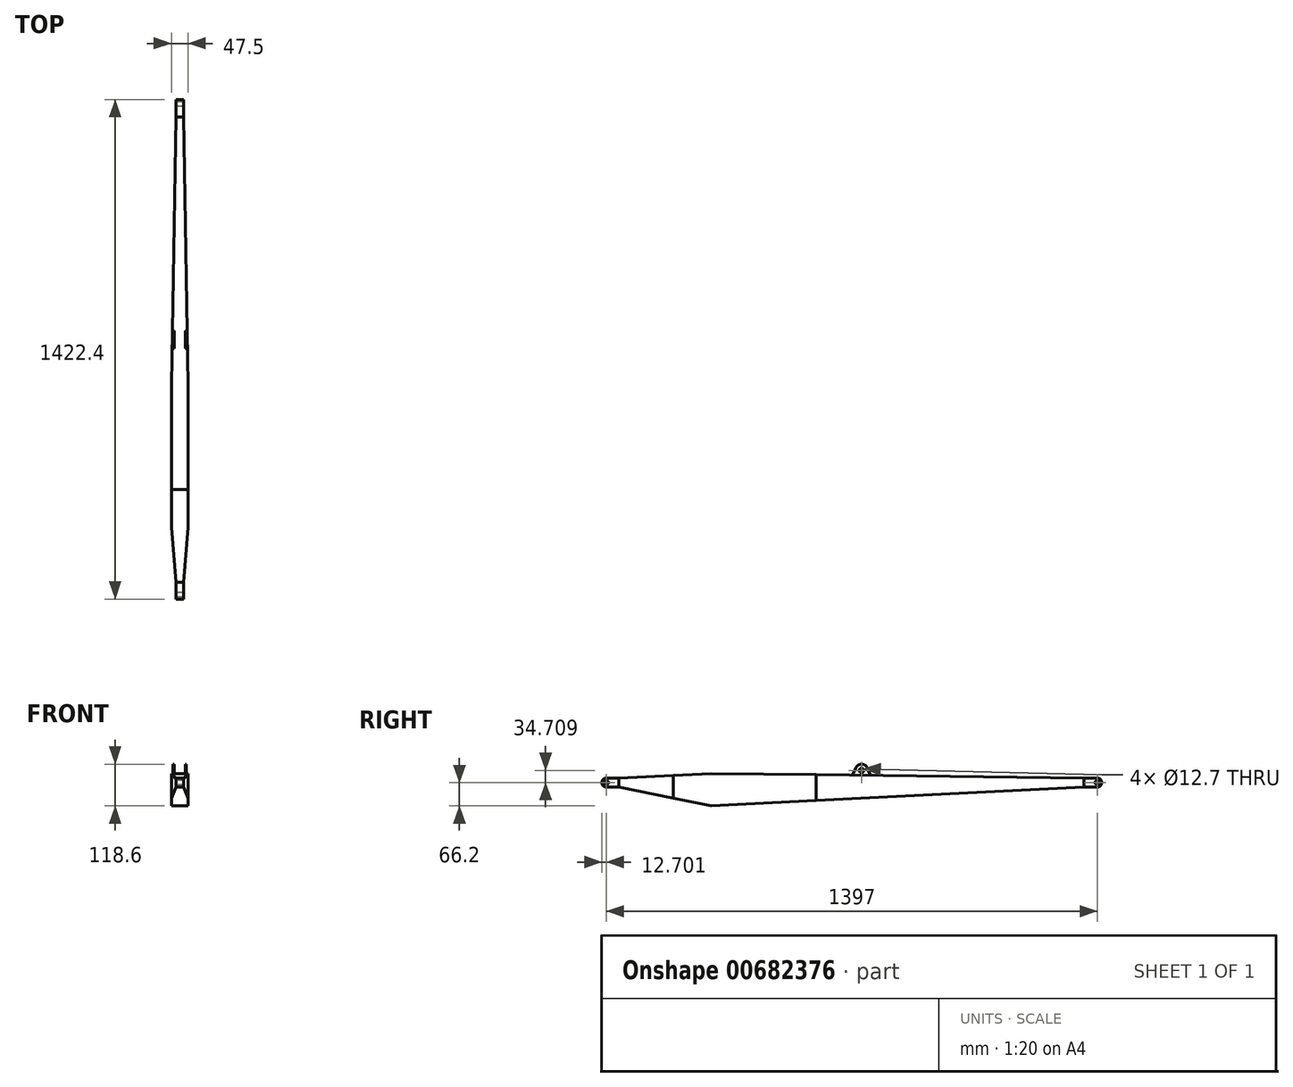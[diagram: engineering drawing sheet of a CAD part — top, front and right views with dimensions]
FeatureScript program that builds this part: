
annotation { "Feature Type Name" : "Feature", "Feature Type Description" : "" }
export const myFeature = defineFeature(function(context is Context, id is Id, definition is map)
    precondition{}
    {
        {
            var Q0;
            Q0=qCreatedBy(makeId("Right.planeOp"),FACE);
            var sketch = newSketch(context, id + "F0", { "sketchPlane" : qUnion([Q0])});
            skCircle(sketch, "E0", {"center": v(-27.04, 0) * mm, "radius": 6.35 * mm});
            skLineSegment(sketch, "E1", {"start": v(-27.04, 0) * mm, "end": v(1369.96, 0) * mm, "construction": true});
            skCircle(sketch, "E2", {"center": v(1369.96, 0) * mm, "radius": 6.35 * mm});
            skArc(sketch, "E3", {"start": v(-27.04, 12.7) * mm, "mid": v(-39.74, 0) * mm, "end": v(-27.04, -12.7) * mm});
            skArc(sketch, "E4", {"start": v(1369.96, -12.7) * mm, "mid": v(1382.66, 0) * mm, "end": v(1369.96, 12.7) * mm});
            skLineSegment(sketch, "E5", {"start": v(-27.04, 12.7) * mm, "end": v(1369.96, 12.7) * mm});
            skLineSegment(sketch, "E6.MirrorCS", {"start": v(-27.04, -12.7) * mm, "end": v(1369.96, -12.7) * mm});
            skSolve(sketch);
        }
        {
            var Q0;
            Q0=makeQuery(id+"F0.imprint","IMPRINT",FACE,{"disambiguationData":[TD([[makeQuery(id+"F0.imprint","IMPRINT",EDGE,{"derivedFrom":sQuery(id+"F0.wireOp",EDGE,"E0")}),-1.0]])]});
            extrude(context, id + "F1", {"entities" : qUnion([Q0]), "endBound" : BoundingType.SYMMETRIC, "depth" : 22.1 * mm, "offsetDistance" : 25.4 * mm});
        }
        {
            var Q0;
            Q0=makeQuery(id+"F1.opExtrude","CAP_FACE",FACE,{"disambiguationData":[OSD([sQuery(id+"F0.wireOp",EDGE,"E0"),sQuery(id+"F0.wireOp",EDGE,"E2"),sQuery(id+"F0.wireOp",EDGE,"E3"),sQuery(id+"F0.wireOp",EDGE,"E4"),sQuery(id+"F0.wireOp",EDGE,"E5"),sQuery(id+"F0.wireOp",EDGE,"E6.MirrorCS")])],"isStart":false});
            var sketch = newSketch(context, id + "F2", { "sketchPlane" : qUnion([Q0])});
            skLineSegment(sketch, "E7", {"start": v(8.23, -12.7) * mm, "end": v(271.92, -66.2) * mm});
            skLineSegment(sketch, "E8", {"start": v(271.92, -66.2) * mm, "end": v(1332.15, -12.7) * mm});
            skSolve(sketch);
        }
        {
            var Q0;
            {var subQ0=sQuery(id+"F2.wireOp",EDGE,"E7");Q0=makeQuery(id+"F2.imprint","IMPRINT",FACE,{"disambiguationData":[TD([[makeQuery(id+"F2.imprint","IMPRINT",EDGE,{"derivedFrom":subQ0}),1.0]])]});}
            var Q1;
            Q1=makeQuery(id+"F1.opExtrude","CAP_FACE",FACE,{"disambiguationData":[OSD([sQuery(id+"F0.wireOp",EDGE,"E0"),sQuery(id+"F0.wireOp",EDGE,"E2"),sQuery(id+"F0.wireOp",EDGE,"E3"),sQuery(id+"F0.wireOp",EDGE,"E4"),sQuery(id+"F0.wireOp",EDGE,"E5"),sQuery(id+"F0.wireOp",EDGE,"E6.MirrorCS")])],"isStart":true});
            extrude(context, id + "F3", {"entities" : qUnion([Q0]), "operationType" : NewBodyOperationType.ADD, "endBound" : BoundingType.UP_TO_SURFACE, "oppositeDirection" : true, "depth" : 25.4 * mm, "endBoundEntityFace" : qUnion([Q1]), "offsetDistance" : 25.4 * mm});
        }
        {
            var Q0;
            {var subQ0=sQuery(id+"F0.wireOp",EDGE,"E6.MirrorCS");Q0=makeQuery(id+"F3.boolean.opBoolean","MERGE",FACE,{"derivedFrom":[makeQuery(id+"F1.opExtrude","CAP_FACE",FACE,{"disambiguationData":[OSD([sQuery(id+"F0.wireOp",EDGE,"E0"),sQuery(id+"F0.wireOp",EDGE,"E2"),sQuery(id+"F0.wireOp",EDGE,"E3"),sQuery(id+"F0.wireOp",EDGE,"E4"),sQuery(id+"F0.wireOp",EDGE,"E5"),subQ0])],"isStart":false}),makeQuery(id+"F3.opExtrude","CAP_FACE",FACE,{"disambiguationData":[OSD([subQ0,sQuery(id+"F2.wireOp",EDGE,"E7"),sQuery(id+"F2.wireOp",EDGE,"E8")])],"isStart":true})]});}
            var sketch = newSketch(context, id + "F4", { "sketchPlane" : qUnion([Q0])});
            skLineSegment(sketch, "E9", {"start": v(8.23, 12.7) * mm, "end": v(271.92, 26) * mm});
            skLineSegment(sketch, "E10", {"start": v(271.92, 26) * mm, "end": v(1332.15, 12.7) * mm});
            skLineSegment(sketch, "E11", {"start": v(8.23, 12.7) * mm, "end": v(8.23, -12.7) * mm});
            skLineSegment(sketch, "E12", {"start": v(8.23, -12.7) * mm, "end": v(271.92, -66.2) * mm});
            skLineSegment(sketch, "E13", {"start": v(271.92, -66.2) * mm, "end": v(1332.15, -12.7) * mm});
            skLineSegment(sketch, "E14", {"start": v(1332.15, -12.7) * mm, "end": v(1332.15, 12.7) * mm});
            skSolve(sketch);
        }
        {
            var Q0;
            {var subQ1=sQuery(id+"F4.wireOp",EDGE,"E11");Q0=makeQuery(id+"F4.imprint","IMPRINT",FACE,{"disambiguationData":[TD([[makeQuery(id+"F4.imprint","IMPRINT",EDGE,{"derivedFrom":subQ1}),1.0]])]});}
            var Q1;
            {var subQ0=sQuery(id+"F4.wireOp",EDGE,"E9");Q1=makeQuery(id+"F4.imprint","IMPRINT",FACE,{"disambiguationData":[TD([[makeQuery(id+"F4.imprint","IMPRINT",EDGE,{"derivedFrom":subQ0}),-1.0]])]});}
            extrude(context, id + "F5", {"entities" : qUnion([Q0, Q1]), "operationType" : NewBodyOperationType.ADD, "depth" : 12.7 * mm, "offsetDistance" : 25.4 * mm});
        }
        {
            var Q0;
            Q0=makeQuery(id+"F5.opExtrude","CAP_FACE",FACE,{"disambiguationData":[OSD([sQuery(id+"F4.wireOp",EDGE,"E9"),sQuery(id+"F4.wireOp",EDGE,"E10"),sQuery(id+"F4.wireOp",EDGE,"E11"),sQuery(id+"F4.wireOp",EDGE,"E12"),sQuery(id+"F4.wireOp",EDGE,"E13"),sQuery(id+"F4.wireOp",EDGE,"E14")])],"isStart":true});
            var Q1;
            {var subQ0=sQuery(id+"F0.wireOp",EDGE,"E6.MirrorCS");var subQ1=sQuery(id+"F0.wireOp",EDGE,"E5");var subQ2=sQuery(id+"F0.wireOp",EDGE,"E4");var subQ3=sQuery(id+"F0.wireOp",EDGE,"E3");var subQ4=sQuery(id+"F0.wireOp",EDGE,"E2");var subQ5=sQuery(id+"F0.wireOp",EDGE,"E0");Q1=makeQuery(id+"F3.boolean.opBoolean","MERGE",FACE,{"derivedFrom":[makeQuery(id+"F1.opExtrude","CAP_FACE",FACE,{"disambiguationData":[OSD([subQ5,subQ4,subQ3,subQ2,subQ1,subQ0])],"isStart":true}),makeQuery(id+"F3.opExtrude","CAP_FACE",FACE,{"disambiguationData":[OSD([subQ5,subQ4,subQ3,subQ2,subQ1,subQ0])],"isStart":false})]});}
            extrude(context, id + "F6", {"entities" : qUnion([Q0]), "operationType" : NewBodyOperationType.ADD, "endBound" : BoundingType.UP_TO_SURFACE, "depth" : 25.4 * mm, "endBoundEntityFace" : qUnion([Q1]), "offsetDistance" : 25.4 * mm});
        }
        {
            var Q0;
            {var subQ0=sQuery(id+"F0.wireOp",EDGE,"E6.MirrorCS");var subQ1=sQuery(id+"F0.wireOp",EDGE,"E5");var subQ2=sQuery(id+"F0.wireOp",EDGE,"E4");var subQ3=sQuery(id+"F0.wireOp",EDGE,"E3");var subQ4=sQuery(id+"F0.wireOp",EDGE,"E2");var subQ5=sQuery(id+"F0.wireOp",EDGE,"E0");Q0=makeQuery(id+"F6.boolean.opBoolean","MERGE",FACE,{"derivedFrom":[makeQuery(id+"F3.boolean.opBoolean","MERGE",FACE,{"derivedFrom":[makeQuery(id+"F1.opExtrude","CAP_FACE",FACE,{"disambiguationData":[OSD([subQ5,subQ4,subQ3,subQ2,subQ1,subQ0])],"isStart":true}),makeQuery(id+"F3.opExtrude","CAP_FACE",FACE,{"disambiguationData":[OSD([subQ5,subQ4,subQ3,subQ2,subQ1,subQ0])],"isStart":false})]}),makeQuery(id+"F6.opExtrude","CAP_FACE",FACE,{"disambiguationData":[OSD([subQ5,subQ4,subQ3,subQ2,subQ1,subQ0])],"isStart":false})]});}
            var sketch = newSketch(context, id + "F7", { "sketchPlane" : qUnion([Q0])});
            skLineSegment(sketch, "E15.0", {"start": v(-1332.15, -12.7) * mm, "end": v(-1332.15, 12.7) * mm});
            skLineSegment(sketch, "E16.0", {"start": v(-8.23, 12.7) * mm, "end": v(-8.23, -12.7) * mm});
            skLineSegment(sketch, "E17.0.0", {"start": v(-8.23, -12.7) * mm, "end": v(27.04, -12.7) * mm});
            skArc(sketch, "E17.0.1", {"start": v(27.04, -12.7) * mm, "mid": v(39.74, 0) * mm, "end": v(27.04, 12.7) * mm});
            skLineSegment(sketch, "E17.0.2", {"start": v(27.04, 12.7) * mm, "end": v(-8.23, 12.7) * mm});
            skLineSegment(sketch, "E17.0.3", {"start": v(-8.23, 12.7) * mm, "end": v(-271.92, 26) * mm});
            skLineSegment(sketch, "E17.0.4", {"start": v(-271.92, 26) * mm, "end": v(-1332.15, 12.7) * mm});
            skLineSegment(sketch, "E17.0.5", {"start": v(-1332.15, 12.7) * mm, "end": v(-1369.96, 12.7) * mm});
            skArc(sketch, "E17.0.6", {"start": v(-1369.96, 12.7) * mm, "mid": v(-1382.66, 0) * mm, "end": v(-1369.96, -12.7) * mm});
            skLineSegment(sketch, "E17.0.7", {"start": v(-1369.96, -12.7) * mm, "end": v(-1332.15, -12.7) * mm});
            skLineSegment(sketch, "E17.0.8", {"start": v(-1332.15, -12.7) * mm, "end": v(-271.92, -66.2) * mm});
            skLineSegment(sketch, "E17.0.9", {"start": v(-271.92, -66.2) * mm, "end": v(-8.23, -12.7) * mm});
            skSolve(sketch);
        }
        {
            var Q0;
            Q0=makeQuery(id+"F7.imprint","IMPRINT",FACE,{"disambiguationData":[TD([[makeQuery(id+"F7.imprint","IMPRINT",EDGE,{"derivedFrom":sQuery(id+"F7.wireOp",EDGE,"E15.0")}),-1.0]])]});
            extrude(context, id + "F8", {"entities" : qUnion([Q0]), "operationType" : NewBodyOperationType.ADD, "depth" : 12.7 * mm, "offsetDistance" : 25.4 * mm});
        }
        {
            var Q0;
            Q0=qCreatedBy(makeId("Top.planeOp"),FACE);
            var sketch = newSketch(context, id + "F9", { "sketchPlane" : qUnion([Q0])});
            skPoint(sketch, "E18", {"position": v(-11.05, 1332.15) * mm});
            skLineSegment(sketch, "E19", {"start": v(-11.05, 1332.15) * mm, "end": v(-23.75, 570.25) * mm});
            skLineSegment(sketch, "E20.MirrorCS", {"start": v(11.05, 1332.15) * mm, "end": v(23.75, 570.25) * mm});
            skPoint(sketch, "E21", {"position": v(11.05, 8.23) * mm});
            skPoint(sketch, "E22", {"position": v(-11.05, 8.23) * mm});
            skLineSegment(sketch, "E23", {"start": v(-11.05, 8.23) * mm, "end": v(-23.75, 163.85) * mm});
            skLineSegment(sketch, "E24.MirrorCS", {"start": v(11.05, 8.23) * mm, "end": v(23.75, 163.85) * mm});
            skLineSegment(sketch, "E25", {"start": v(-23.75, 570.25) * mm, "end": v(-23.75, 163.85) * mm});
            skLineSegment(sketch, "E26", {"start": v(23.75, 570.25) * mm, "end": v(23.75, 163.85) * mm});
            skLineSegment(sketch, "E27", {"start": v(-11.05, 8.23) * mm, "end": v(11.05, 8.23) * mm});
            skLineSegment(sketch, "E28", {"start": v(-11.05, 1332.15) * mm, "end": v(-42.65, 1362.9) * mm});
            skLineSegment(sketch, "E29", {"start": v(-42.65, 1362.9) * mm, "end": v(-507.55, 214.96) * mm});
            skLineSegment(sketch, "E30", {"start": v(-507.55, 214.96) * mm, "end": v(-61.7, -33.6) * mm});
            skLineSegment(sketch, "E31", {"start": v(-61.7, -33.6) * mm, "end": v(-11.05, 8.23) * mm});
            skLineSegment(sketch, "E32.MirrorCS", {"start": v(61.7, -33.6) * mm, "end": v(11.05, 8.23) * mm});
            skLineSegment(sketch, "E33.MirrorCS", {"start": v(507.55, 214.96) * mm, "end": v(61.7, -33.6) * mm});
            skLineSegment(sketch, "E34.MirrorCS", {"start": v(42.65, 1362.9) * mm, "end": v(507.55, 214.96) * mm});
            skLineSegment(sketch, "E35.MirrorCS", {"start": v(11.05, 1332.15) * mm, "end": v(42.65, 1362.9) * mm});
            skSolve(sketch);
        }
        {
            var Q0;
            Q0=makeQuery(id+"F9.imprint","IMPRINT",FACE,{"disambiguationData":[TD([[makeQuery(id+"F9.imprint","IMPRINT",EDGE,{"derivedFrom":sQuery(id+"F9.wireOp",EDGE,"E19")}),-1.0]])]});
            var Q1;
            Q1=makeQuery(id+"F9.imprint","IMPRINT",FACE,{"disambiguationData":[TD([[makeQuery(id+"F9.imprint","IMPRINT",EDGE,{"derivedFrom":sQuery(id+"F9.wireOp",EDGE,"E20.MirrorCS")}),1.0]])]});
            extrude(context, id + "F10", {"entities" : qUnion([Q0, Q1]), "operationType" : NewBodyOperationType.REMOVE, "endBound" : BoundingType.SYMMETRIC, "oppositeDirection" : true, "depth" : 457.2 * mm, "offsetDistance" : 25.4 * mm});
        }
        {
            var Q0;
            {var subQ0=sQuery(id+"F4.wireOp",EDGE,"E10");Q0=makeQuery(id+"F8.boolean.opBoolean","MERGE",FACE,{"derivedFrom":[makeQuery(id+"F6.boolean.opBoolean","MERGE",FACE,{"derivedFrom":[makeQuery(id+"F5.opExtrude","SWEPT_FACE",FACE,{"disambiguationData":[OSD([subQ0])]}),makeQuery(id+"F6.opExtrude","SWEPT_FACE",FACE,{"disambiguationData":[OSD([subQ0])]})]}),makeQuery(id+"F8.opExtrude","SWEPT_FACE",FACE,{"disambiguationData":[OSD([sQuery(id+"F7.wireOp",EDGE,"E17.0.4")])]})]});}
            var sketch = newSketch(context, id + "F11", { "sketchPlane" : qUnion([Q0])});
            skLineSegment(sketch, "E36", {"start": v(-15.88, 723.73) * mm, "end": v(-15.88, 672.93) * mm});
            skLineSegment(sketch, "E37", {"start": v(0, 723.73) * mm, "end": v(0, 615.57) * mm, "construction": true});
            skLineSegment(sketch, "E38.MirrorCS", {"start": v(15.87, 723.73) * mm, "end": v(15.87, 672.93) * mm});
            skLineSegment(sketch, "E39", {"start": v(-15.88, 672.93) * mm, "end": v(-19.05, 672.93) * mm});
            skLineSegment(sketch, "E40", {"start": v(-19.05, 672.93) * mm, "end": v(-19.05, 723.73) * mm});
            skLineSegment(sketch, "E41.MirrorCS", {"start": v(19.05, 672.93) * mm, "end": v(19.05, 723.73) * mm});
            skLineSegment(sketch, "E42.MirrorCS", {"start": v(15.87, 672.93) * mm, "end": v(19.05, 672.93) * mm});
            skLineSegment(sketch, "E43", {"start": v(-21.19, 723.73) * mm, "end": v(21.19, 723.73) * mm});
            skSolve(sketch);
        }
        {
            var Q0;
            {var subQ0=sQuery(id+"F11.wireOp",EDGE,"E36");Q0=makeQuery(id+"F11.imprint","IMPRINT",FACE,{"disambiguationData":[TD([[makeQuery(id+"F11.imprint","IMPRINT",EDGE,{"derivedFrom":subQ0}),-1.0]])]});}
            var Q1;
            {var subQ0=sQuery(id+"F11.wireOp",EDGE,"E38.MirrorCS");Q1=makeQuery(id+"F11.imprint","IMPRINT",FACE,{"disambiguationData":[TD([[makeQuery(id+"F11.imprint","IMPRINT",EDGE,{"derivedFrom":subQ0}),1.0]])]});}
            extrude(context, id + "F12", {"entities" : qUnion([Q0, Q1]), "operationType" : NewBodyOperationType.ADD, "depth" : 31.75 * mm, "offsetDistance" : 25.4 * mm});
        }
        {
            var Q0;
            Q0=makeQuery(id+"F12.opExtrude","SWEPT_FACE",FACE,{"disambiguationData":[OSD([sQuery(id+"F11.wireOp",EDGE,"E41.MirrorCS")])]});
            var sketch = newSketch(context, id + "F13", { "sketchPlane" : qUnion([Q0])});
            skLineSegment(sketch, "E44", {"start": v(673.25, 20.97) * mm, "end": v(683.2, 42.57) * mm});
            skLineSegment(sketch, "E45", {"start": v(687.8, 52.54) * mm, "end": v(699.05, 52.4) * mm, "construction": true});
            skLineSegment(sketch, "E46", {"start": v(699.05, 52.4) * mm, "end": v(699.05, 70.34) * mm, "construction": true});
            skLineSegment(sketch, "E47.MirrorCS", {"start": v(724.84, 20.97) * mm, "end": v(714.9, 42.57) * mm});
            skArc(sketch, "E48", {"start": v(714.9, 42.57) * mm, "mid": v(699.05, 52.4) * mm, "end": v(683.2, 42.57) * mm});
            skPoint(sketch, "E49.orphan", {"position": v(710.3, 52.54) * mm});
            skPoint(sketch, "E50.orphan", {"position": v(715.32, 41.64) * mm});
            skPoint(sketch, "E51.orphan", {"position": v(682.77, 41.64) * mm});
            skCircle(sketch, "E52", {"center": v(699.05, 34.7) * mm, "radius": 6.35 * mm});
            skSolve(sketch);
        }
        {
            var Q0;
            {var subQ0=sQuery(id+"F13.wireOp",EDGE,"E44");Q0=makeQuery(id+"F13.imprint","IMPRINT",FACE,{"disambiguationData":[TD([[makeQuery(id+"F13.imprint","IMPRINT",EDGE,{"derivedFrom":subQ0}),1.0]])]});}
            var Q1;
            Q1=makeQuery(id+"F13.imprint","IMPRINT",FACE,{"disambiguationData":[TD([[makeQuery(id+"F13.imprint","IMPRINT",EDGE,{"derivedFrom":sQuery(id+"F13.wireOp",EDGE,"E52")}),1.0]])]});
            var Q2;
            {var subQ0=sQuery(id+"F13.wireOp",EDGE,"E48");var subQ1=sQuery(id+"F13.wireOp",EDGE,"E47.MirrorCS");var subQ2=makeQuery(id+"F13.imprint","INTERSECT",VERTEX,{"derivedFrom":[subQ1,subQ0]});Q2=makeQuery(id+"F13.imprint","IMPRINT",FACE,{"disambiguationData":[TD([[makeQuery(id+"F13.imprint","IMPRINT",EDGE,{"disambiguationData":[TD([[subQ2,-1.0]])],"derivedFrom":subQ0}),-1.0]])]});}
            extrude(context, id + "F14", {"entities" : qUnion([Q0, Q1, Q2]), "operationType" : NewBodyOperationType.REMOVE, "endBound" : BoundingType.THROUGH_ALL, "oppositeDirection" : true, "depth" : 25.4 * mm, "offsetDistance" : 25.4 * mm});
        }
    });
